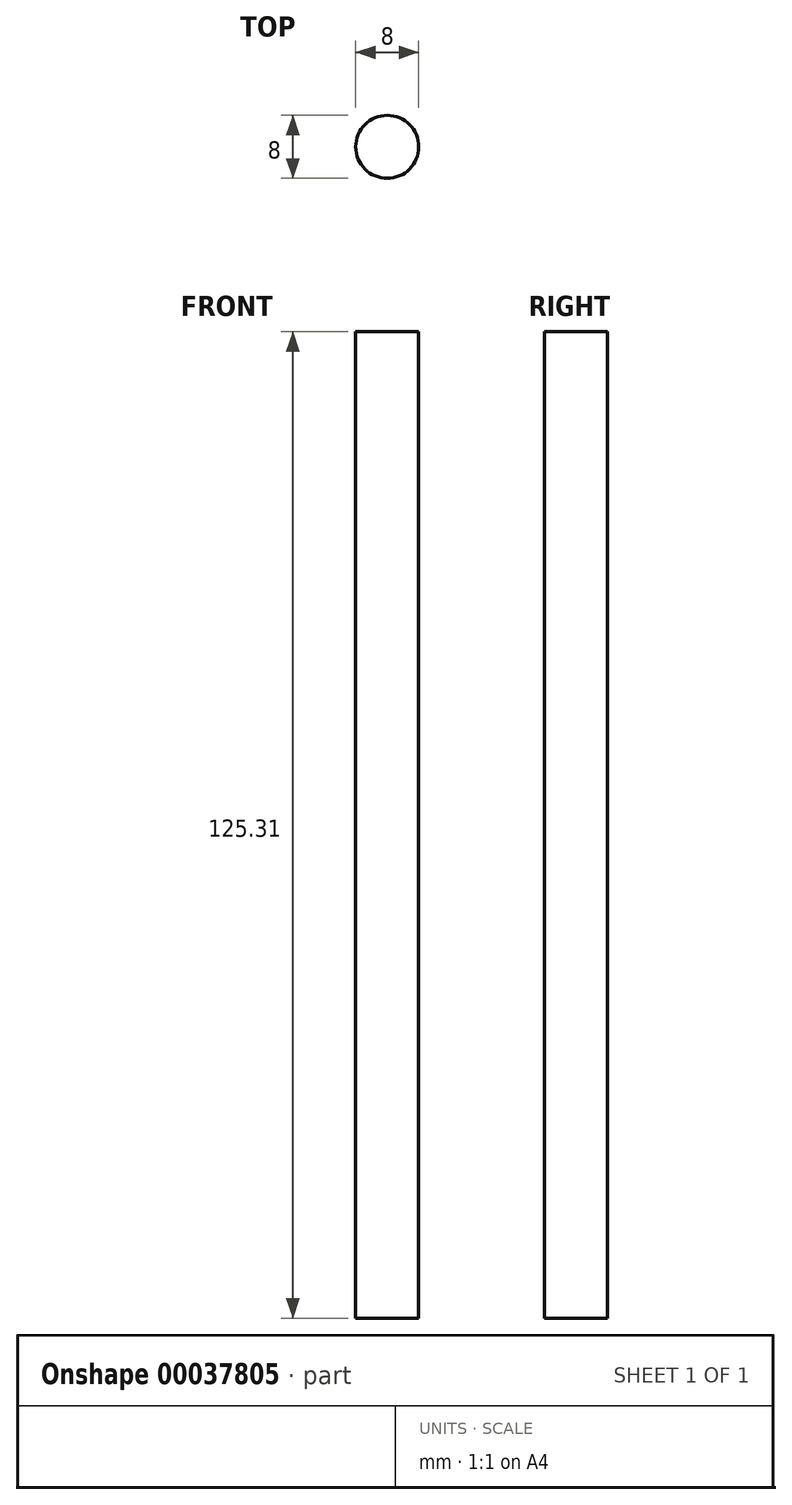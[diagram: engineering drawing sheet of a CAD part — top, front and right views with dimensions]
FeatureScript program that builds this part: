
annotation { "Feature Type Name" : "Feature", "Feature Type Description" : "" }
export const myFeature = defineFeature(function(context is Context, id is Id, definition is map)
    precondition{}
    {
        {
            var Q0;
            Q0=qCreatedBy(makeId("Top.planeOp"),FACE);
            var sketch = newSketch(context, id + "F0", { "sketchPlane" : qUnion([Q0])});
            skCircle(sketch, "E0", {"center": v(0, 0) * mm, "radius": 4 * mm});
            skSolve(sketch);
        }
        {
            var Q0;
            Q0=qSketchRegion(id+"F0",true);
            extrude(context, id + "F1", {"entities" : qUnion([Q0]), "depth" : 125.3 * mm});
        }
    });
